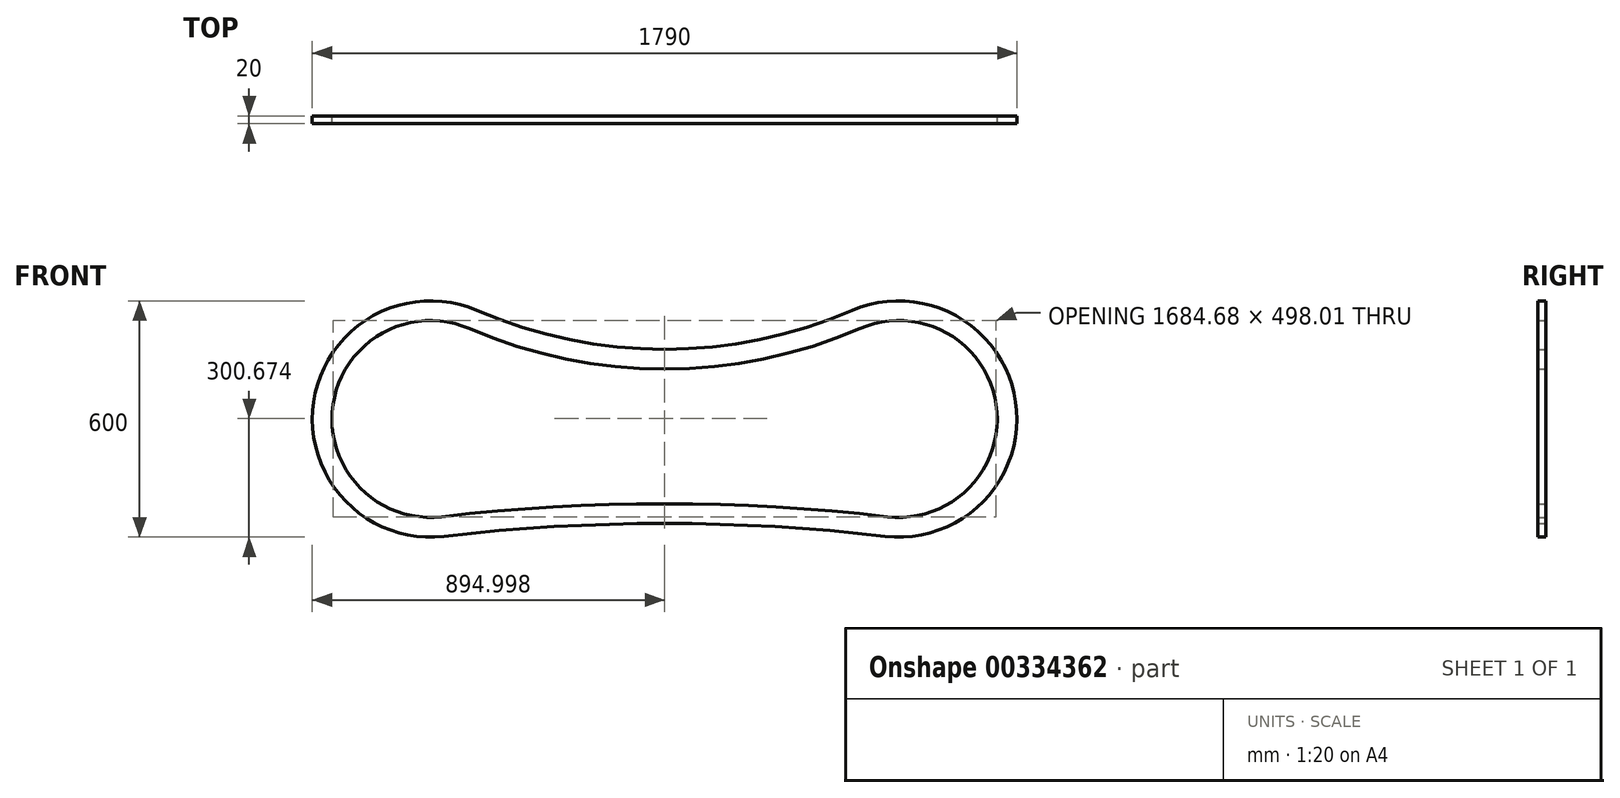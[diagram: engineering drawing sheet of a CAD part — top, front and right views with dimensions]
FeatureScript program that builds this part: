
annotation { "Feature Type Name" : "Feature", "Feature Type Description" : "" }
export const myFeature = defineFeature(function(context is Context, id is Id, definition is map)
    precondition{}
    {
        {
            var Q0;
            Q0=qCreatedBy(makeId("Front.planeOp"),FACE);
            var sketch = newSketch(context, id + "F0", { "sketchPlane" : qUnion([Q0])});
            skArc(sketch, "E0", {"start": v(-4298.58, 2707.71) * mm, "mid": v(-4714.39, 2475.98) * mm, "end": v(-4382.92, 2134.33) * mm});
            skArc(sketch, "E1", {"start": v(-3262.24, 2134.33) * mm, "mid": v(-2930.78, 2475.98) * mm, "end": v(-3346.58, 2707.71) * mm});
            skLineSegment(sketch, "E2", {"start": v(-4417.58, 2432.33) * mm, "end": v(-3227.58, 2432.33) * mm, "construction": true});
            skPoint(sketch, "E3.centerSnap0", {"position": v(-3822.58, 2432.33) * mm});
            skArc(sketch, "E4", {"start": v(-3262.24, 2134.33) * mm, "mid": v(-3822.58, 2166.81) * mm, "end": v(-4382.92, 2134.33) * mm});
            skArc(sketch, "E5", {"start": v(-4298.58, 2707.71) * mm, "mid": v(-3822.58, 2609.27) * mm, "end": v(-3346.58, 2707.71) * mm});
            skArc(sketch, "E6.0", {"start": v(-4318.42, 2661.82) * mm, "mid": v(-4664.92, 2468.7) * mm, "end": v(-4388.7, 2184) * mm});
            skArc(sketch, "E6.1", {"start": v(-4318.42, 2661.82) * mm, "mid": v(-3822.58, 2559.27) * mm, "end": v(-3326.75, 2661.82) * mm});
            skArc(sketch, "E6.2", {"start": v(-3256.47, 2184) * mm, "mid": v(-2980.24, 2468.7) * mm, "end": v(-3326.75, 2661.82) * mm});
            skArc(sketch, "E6.3", {"start": v(-3256.47, 2184) * mm, "mid": v(-3822.58, 2216.81) * mm, "end": v(-4388.7, 2184) * mm});
            skLineSegment(sketch, "E7", {"start": v(-4382.92, 2134.33) * mm, "end": v(-3262.24, 2134.33) * mm});
            skSolve(sketch);
        }
        {
            var Q0;
            Q0=makeQuery(id+"F0.imprint","IMPRINT",FACE,{"disambiguationData":[TD([[makeQuery(id+"F0.imprint","IMPRINT",EDGE,{"derivedFrom":sQuery(id+"F0.wireOp",EDGE,"E0")}),1.0]])]});
            extrude(context, id + "F1", {"entities" : qUnion([Q0]), "depth" : 20 * mm});
        }
    });
